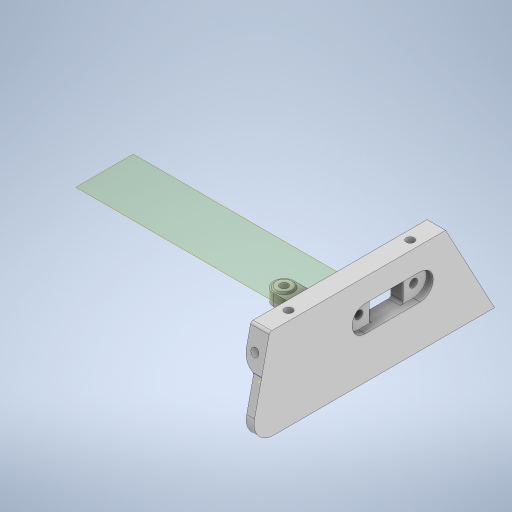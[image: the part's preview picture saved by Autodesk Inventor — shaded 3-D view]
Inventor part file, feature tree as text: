
AUTODESK INVENTOR PART (.ipt)
format: ipt  version: 2023 (Build 270158000, 158)  size: 706,048 bytes
history: native  units: mm
features: extrude x25, sketch x25, other x12, reference x10, projected_geometry x9, fillet x8, chamfer x1
ambient origin geometry x8: Origin, YZ Plane, XZ Plane, XY Plane, X Axis, Y Axis, Z Axis, Center Point
bodies: Body1 (feature_tree)
feature tree (90):
  other  "Bryła1"
  extrude  "Wyciągnięcie proste1"  Depth=6.5mm TaperAngle=0.0deg
  extrude  "Wyciągnięcie proste2"  Depth=3.7mm TaperAngle=0.0deg
  extrude  "Wyciągnięcie proste3"  Depth=1.5mm TaperAngle=0.0deg
  extrude  "Wyciągnięcie proste4"  Depth=6.0mm
  extrude  "Wyciągnięcie proste5"  Depth=3.0mm TaperAngle=0.0deg
  extrude  "Wyciągnięcie proste6"  Depth=5.0mm
  extrude  "Wyciągnięcie proste7"  Depth=3.0mm
  fillet  "Zaokrąglenie1"  Radius=15.0mm
  extrude  "Wyciągnięcie proste8"  Depth=6.0mm
  fillet  "Zaokrąglenie2"  Radius=15.0mm
  fillet  "Zaokrąglenie3"  Radius=35.5mm
  extrude  "Wyciągnięcie proste9"  TaperAngle=0.0deg  [1 undecoded]
  extrude  "Wyciągnięcie proste10"  Depth=5.0mm
  other  "Płaszczyzna konstrukcyjna1"
  extrude  "Wyciągnięcie proste11"  Depth=10.0mm TaperAngle=0.0deg
  extrude  "Wyciągnięcie proste12"  Depth=3.5mm
  extrude  "Wyciągnięcie proste13"  Depth=2.0mm
  other  "Płaszczyzna konstrukcyjna2"
  extrude  "Wyciągnięcie proste14"  Depth=7.22mm
  extrude  "Wyciągnięcie proste15"  Depth=3.0mm
  chamfer  "Faza1"  Distance=15.0mm
  fillet  "Zaokrąglenie7"  Radius=26.342mm
  fillet  "Zaokrąglenie8"  Radius=3.0mm
  fillet  "Zaokrąglenie9"  Radius=15.0mm
  extrude  "Wyciągnięcie proste16"  [1 undecoded]
  extrude  "Wyciągnięcie proste17"  Depth=5.7mm
  fillet  "Zaokrąglenie10"  Radius=4.0mm
  sketch  "Szkic18"
  other  "Płaszczyzna konstrukcyjna3"
  extrude  "Wyciągnięcie proste18"  Depth=10.0mm
  sketch  "Szkic19"
  extrude  "Wyciągnięcie proste19"  Depth=10.0mm
  extrude  "Wyciągnięcie proste20"  Depth=7.0mm TaperAngle=0.0deg
  fillet  "Zaokrąglenie11"  Radius=7.0mm
  extrude  "Wyciągnięcie proste21"  Depth=8.0mm
  extrude  "Wyciągnięcie proste22"  Depth=5.0mm TaperAngle=0.0deg
  extrude  "Wyciągnięcie proste23"  Depth=7.0mm
  sketch  "Szkic25"
  extrude  "Wyciągnięcie proste24"  Depth=0.5mm TaperAngle=0.0deg
  extrude  "Wyciągnięcie proste25"  Depth=0.5mm TaperAngle=45.0deg
  sketch  "Szkic1"
  sketch  "Szkic2"
  sketch  "Szkic3"
  sketch  "Szkic4"
  sketch  "Szkic5"
  sketch  "Szkic6"
  projected_geometry  "Pętla rzutowana1"
  sketch  "Szkic7"
  sketch  "Szkic8"
  projected_geometry  "Pętla rzutowana2"
  sketch  "Szkic9"
  sketch  "Szkic10"
  sketch  "Szkic11"
  sketch  "Szkic12"
  reference  "Odniesienie1"
  reference  "Odniesienie2"
  sketch  "Szkic13"
  sketch  "Szkic14"
  reference  "Odniesienie3"
  sketch  "Szkic15"
  projected_geometry  "Pętla rzutowana3"
  sketch  "Szkic16"
  projected_geometry  "Pętla rzutowana4"
  sketch  "Szkic17"
  reference  "Odniesienie4"
  reference  "Odniesienie5"
  reference  "Odniesienie6"
  reference  "Odniesienie7"
  projected_geometry  "Pętla rzutowana5"
  sketch  "Szkic20"
  projected_geometry  "Pętla rzutowana6"
  reference  "Odniesienie8"
  sketch  "Szkic21"
  projected_geometry  "Pętla rzutowana7"
  sketch  "Szkic22"
  projected_geometry  "Pętla rzutowana8"
  reference  "Odniesienie9"
  reference  "Odniesienie10"
  sketch  "Szkic23"
  sketch  "Szkic24"
  projected_geometry  "Pętla rzutowana9"
  other  "<userpath>\Desktop\MojeRoboty\Stefan\mechanics 2\STEFAN.iam"
  other  "STEFAN.iam"
  other  "plytka_dol:1"
  other  "ARDUINO_NANO:1"
  other  "board_up:1"
  other  "koło_minisumo:2"
  other  "podstawa:1"
  other  "plug_2:1"
note: 2 required parameter values undecoded (feature->parameter linkage not recoverable at this tier; creation-order binding heuristic only, values carry confidence <= 0.55)
